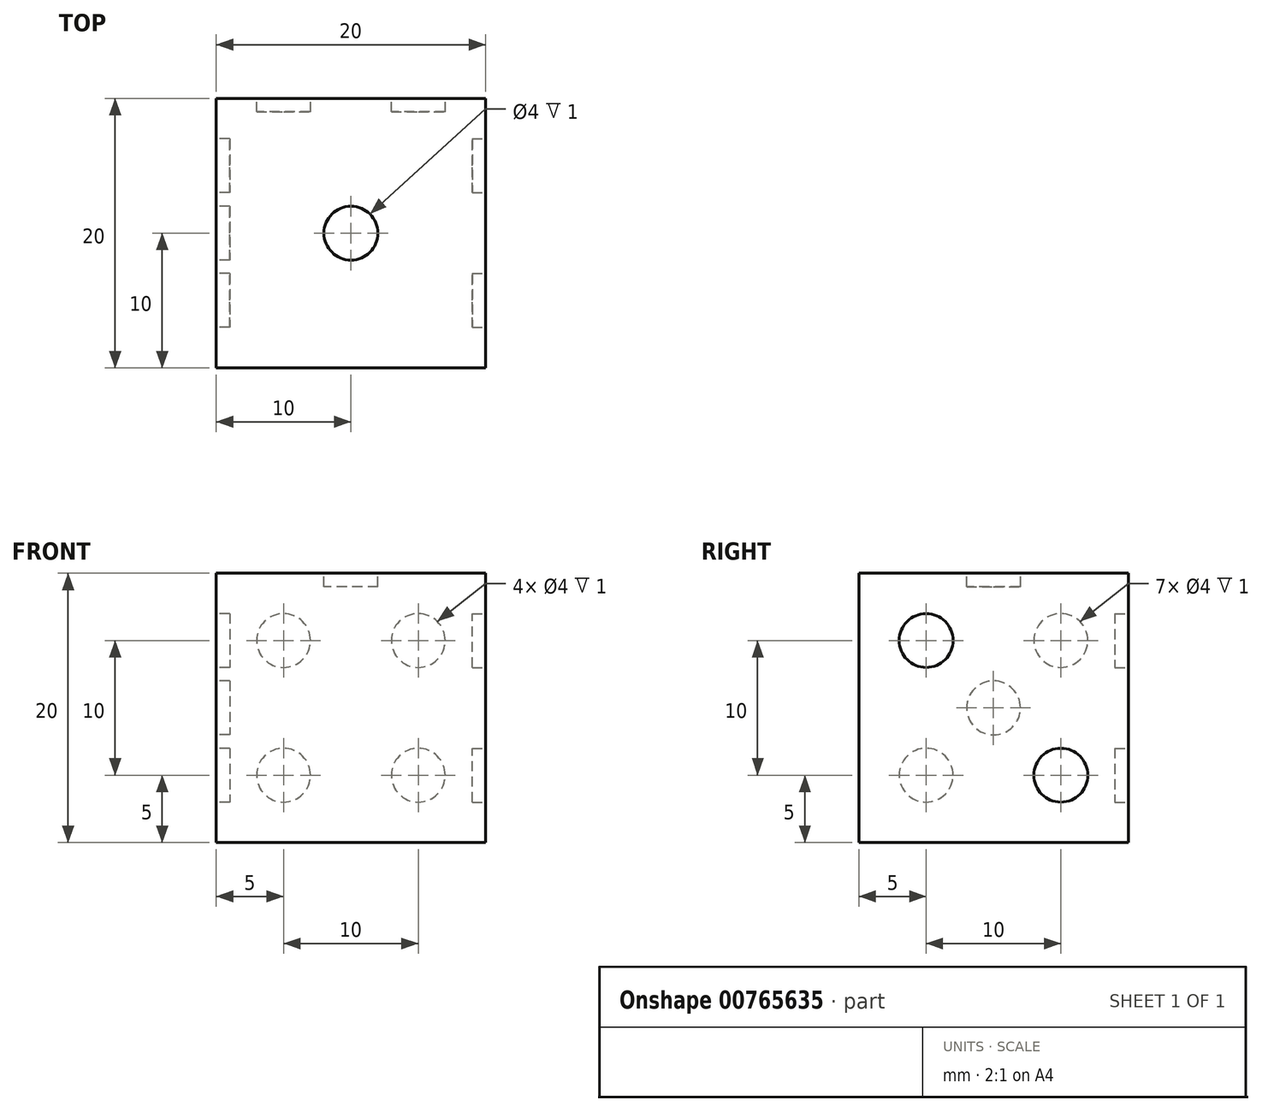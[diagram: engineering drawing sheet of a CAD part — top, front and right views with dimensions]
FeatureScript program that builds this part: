
annotation { "Feature Type Name" : "Feature", "Feature Type Description" : "" }
export const myFeature = defineFeature(function(context is Context, id is Id, definition is map)
    precondition{}
    {
        {
            var Q0;
            Q0=qCreatedBy(makeId("Top.planeOp"),FACE);
            var sketch = newSketch(context, id + "F0", { "sketchPlane" : qUnion([Q0])});
            skLineSegment(sketch, "E0.bottom", {"start": v(0, 0) * mm, "end": v(-20, 0) * mm});
            skLineSegment(sketch, "E0.top", {"start": v(0, 20) * mm, "end": v(-20, 20) * mm});
            skLineSegment(sketch, "E0.left", {"start": v(0, 0) * mm, "end": v(0, 20) * mm});
            skLineSegment(sketch, "E0.right", {"start": v(-20, 0) * mm, "end": v(-20, 20) * mm});
            skSolve(sketch);
        }
        {
            var Q0;
            Q0 = qSketchRegion(id + "F0", true);
            extrude(context, id + "F1", {"entities" : qUnion([Q0]), "depth" : 20 * mm, "offsetDistance" : 25 * mm});
        }
        {
            var Q0;
            Q0=makeQuery(id+"F1.opExtrude","CAP_FACE",FACE,{"disambiguationData":[OSD([sQuery(id+"F0.wireOp",EDGE,"E0.bottom"),sQuery(id+"F0.wireOp",EDGE,"E0.top"),sQuery(id+"F0.wireOp",EDGE,"E0.left"),sQuery(id+"F0.wireOp",EDGE,"E0.right")])],"isStart":false});
            var sketch = newSketch(context, id + "F2", { "sketchPlane" : qUnion([Q0])});
            skLineSegment(sketch, "E1", {"start": v(0, 0) * mm, "end": v(-20, 20) * mm, "construction": true});
            skCircle(sketch, "E2", {"center": v(-10, 10) * mm, "radius": 2 * mm});
            skSolve(sketch);
        }
        {
            var Q0;
            Q0=makeQuery(id+"F1.opExtrude","SWEPT_FACE",FACE,{"disambiguationData":[OSD([sQuery(id+"F0.wireOp",EDGE,"E0.left")])]});
            var sketch = newSketch(context, id + "F3", { "sketchPlane" : qUnion([Q0])});
            skLineSegment(sketch, "E3", {"start": v(20, 20) * mm, "end": v(0, 0) * mm, "construction": true});
            skLineSegment(sketch, "E4", {"start": v(0, 20) * mm, "end": v(10, 10) * mm, "construction": true});
            skLineSegment(sketch, "E5", {"start": v(20, 0) * mm, "end": v(10, 10) * mm, "construction": true});
            skCircle(sketch, "E6", {"center": v(15, 5) * mm, "radius": 2 * mm});
            skCircle(sketch, "E7", {"center": v(5, 15) * mm, "radius": 2 * mm});
            skSolve(sketch);
        }
        {
            var Q0;
            Q0 = qSketchRegion(id + "F2", true);
            extrude(context, id + "F4", {"entities" : qUnion([Q0]), "operationType" : NewBodyOperationType.REMOVE, "oppositeDirection" : true, "depth" : 1 * mm, "offsetDistance" : 25 * mm});
        }
        {
            var Q0;
            Q0 = qSketchRegion(id + "F3", true);
            extrude(context, id + "F5", {"entities" : qUnion([Q0]), "operationType" : NewBodyOperationType.REMOVE, "oppositeDirection" : true, "depth" : 1 * mm, "offsetDistance" : 25 * mm});
        }
        {
            var Q0;
            Q0=makeQuery(id+"F1.opExtrude","SWEPT_FACE",FACE,{"disambiguationData":[OSD([sQuery(id+"F0.wireOp",EDGE,"E0.top")])]});
            var sketch = newSketch(context, id + "F6", { "sketchPlane" : qUnion([Q0])});
            skLineSegment(sketch, "E8", {"start": v(0, 0) * mm, "end": v(10, 10) * mm, "construction": true});
            skLineSegment(sketch, "E9", {"start": v(10, 10) * mm, "end": v(20, 20) * mm, "construction": true});
            skLineSegment(sketch, "E10", {"start": v(10, 10) * mm, "end": v(20, 0) * mm, "construction": true});
            skLineSegment(sketch, "E11", {"start": v(10, 10) * mm, "end": v(0, 20) * mm, "construction": true});
            skCircle(sketch, "E12", {"center": v(15, 5) * mm, "radius": 2 * mm});
            skCircle(sketch, "E13", {"center": v(5, 5) * mm, "radius": 2 * mm});
            skCircle(sketch, "E14", {"center": v(5, 15) * mm, "radius": 2 * mm});
            skCircle(sketch, "E15", {"center": v(15, 15) * mm, "radius": 2 * mm});
            skSolve(sketch);
        }
        {
            var Q0;
            Q0 = qSketchRegion(id + "F6", true);
            extrude(context, id + "F7", {"entities" : qUnion([Q0]), "operationType" : NewBodyOperationType.REMOVE, "oppositeDirection" : true, "depth" : 1 * mm, "offsetDistance" : 25 * mm});
        }
        {
            var Q0;
            Q0=makeQuery(id+"F1.opExtrude","SWEPT_FACE",FACE,{"disambiguationData":[OSD([sQuery(id+"F0.wireOp",EDGE,"E0.right")])]});
            var sketch = newSketch(context, id + "F8", { "sketchPlane" : qUnion([Q0])});
            skCircle(sketch, "E16", {"center": v(-10, 10) * mm, "radius": 2 * mm});
            skLineSegment(sketch, "E17", {"start": v(-20, 0) * mm, "end": v(-10, 10) * mm, "construction": true});
            skLineSegment(sketch, "E18", {"start": v(-10, 10) * mm, "end": v(0, 20) * mm, "construction": true});
            skLineSegment(sketch, "E19", {"start": v(-10, 10) * mm, "end": v(0, 0) * mm, "construction": true});
            skLineSegment(sketch, "E20", {"start": v(-10, 10) * mm, "end": v(-20, 20) * mm, "construction": true});
            skCircle(sketch, "E21", {"center": v(-5, 15) * mm, "radius": 2 * mm});
            skCircle(sketch, "E22", {"center": v(-5, 5) * mm, "radius": 2 * mm});
            skCircle(sketch, "E23", {"center": v(-15, 5) * mm, "radius": 2 * mm});
            skCircle(sketch, "E24", {"center": v(-15, 15) * mm, "radius": 2 * mm});
            skSolve(sketch);
        }
        {
            var Q0;
            Q0 = qSketchRegion(id + "F8", true);
            extrude(context, id + "F9", {"entities" : qUnion([Q0]), "operationType" : NewBodyOperationType.REMOVE, "oppositeDirection" : true, "depth" : 1 * mm, "offsetDistance" : 25 * mm});
        }
    });
